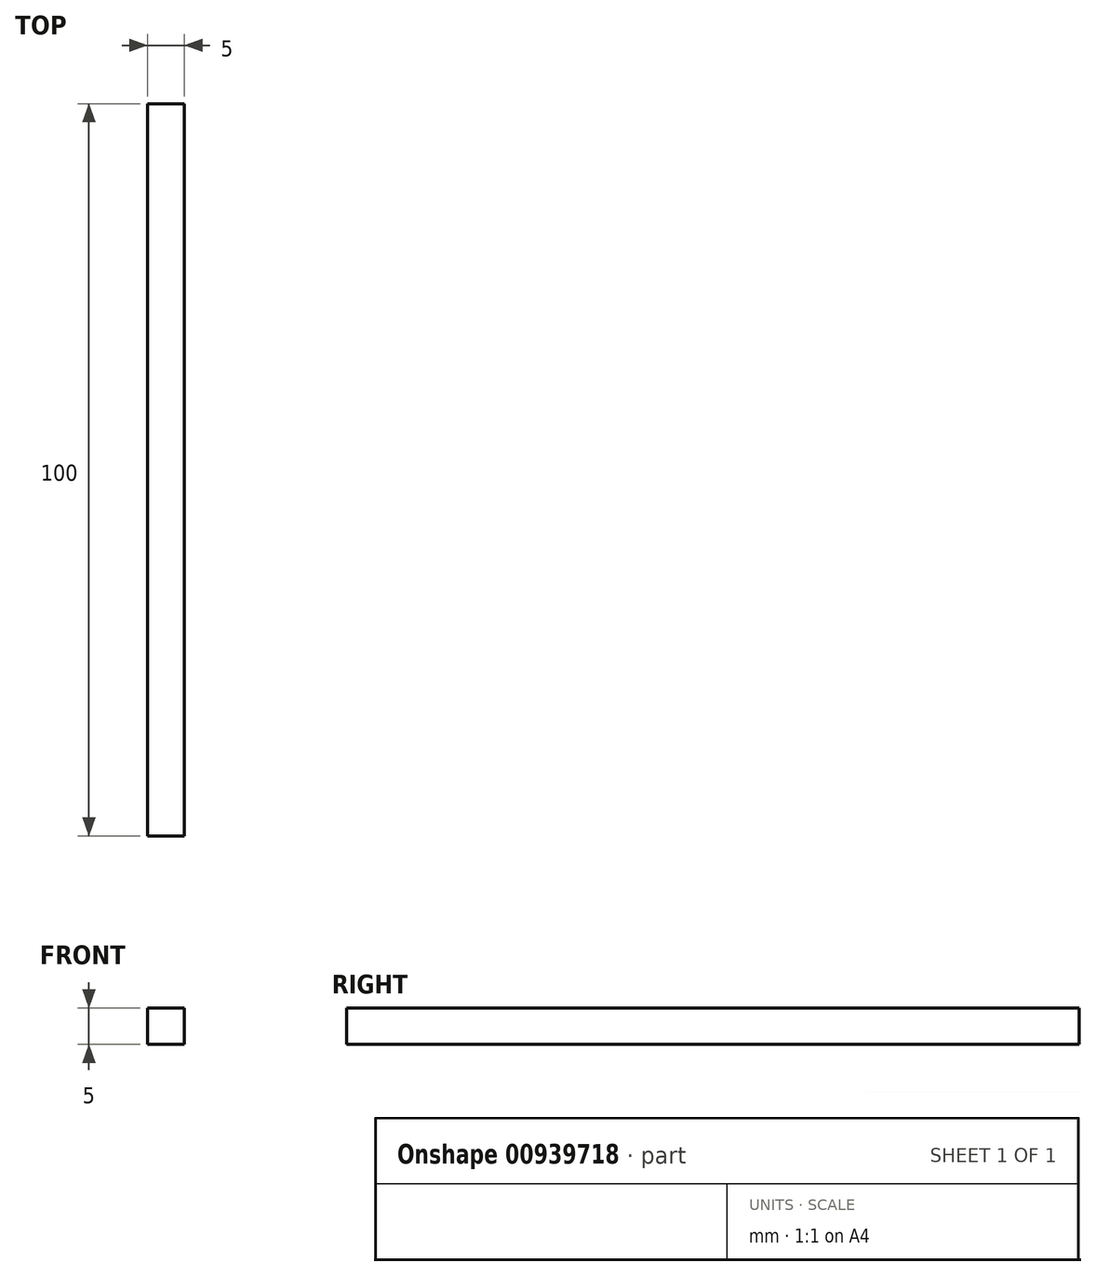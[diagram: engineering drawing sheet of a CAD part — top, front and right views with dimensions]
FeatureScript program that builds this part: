
annotation { "Feature Type Name" : "Feature", "Feature Type Description" : "" }
export const myFeature = defineFeature(function(context is Context, id is Id, definition is map)
    precondition{}
    {
        {
            var Q0;
            Q0=qCreatedBy(makeId("Front.planeOp"),FACE);
            var sketch = newSketch(context, id + "F0", { "sketchPlane" : qUnion([Q0])});
            skLineSegment(sketch, "E0.bottom", {"start": v(0, 0) * mm, "end": v(-5, 0) * mm});
            skLineSegment(sketch, "E0.top", {"start": v(0, 5) * mm, "end": v(-5, 5) * mm});
            skLineSegment(sketch, "E0.left", {"start": v(0, 0) * mm, "end": v(0, 5) * mm});
            skLineSegment(sketch, "E0.right", {"start": v(-5, 0) * mm, "end": v(-5, 5) * mm});
            skSolve(sketch);
        }
        {
            var Q0;
            Q0 = qSketchRegion(id + "F0", true);
            extrude(context, id + "F1", {"entities" : qUnion([Q0]), "depth" : 100 * mm, "offsetDistance" : 25 * mm});
        }
    });
